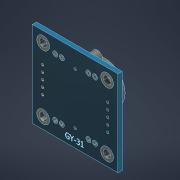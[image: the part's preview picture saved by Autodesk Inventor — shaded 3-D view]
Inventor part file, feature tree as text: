
AUTODESK INVENTOR PART (.ipt)
format: ipt  version: 2021 (Build 250183000, 183)  size: 1,518,592 bytes
history: native  units: mm
features: sketch x20, extrude x14, projected_geometry x8, hole x4, mirror x4, fillet x2, thread x1, plane x1
ambient origin geometry x8: Origin, YZ Plane, XZ Plane, XY Plane, X Axis, Y Axis, Z Axis, Center Point
bodies: Solid1 (feature_tree)
feature tree (54):
  extrude  "Extrusion1"  Depth=33.5mm
  hole  "Hole1"  [1 undecoded]
  extrude  "Extrusion2"  Depth=25.0mm
  extrude  "Extrusion3"  TaperAngle=0.0deg  [1 undecoded]
  hole  "Hole2"  [1 undecoded]
  mirror  "Mirror1"
  extrude  "Extrusion4"  Depth=5.0mm
  mirror  "Mirror2"
  extrude  "Extrusion5"  Depth=5.0mm
  mirror  "Mirror3"
  extrude  "Extrusion6"  Depth=0.01mm TaperAngle=0.0deg
  extrude  "Extrusion7"  Depth=4.0mm
  hole  "Hole3"  [1 undecoded]
  extrude  "Extrusion8"  Depth=2.0mm
  extrude  "Extrusion9"  Depth=2.0mm
  mirror  "Mirror4"
  extrude  "Extrusion10"  Depth=0.01mm TaperAngle=0.0deg
  extrude  "Extrusion11"  Depth=13.0mm
  hole  "Hole4"  [1 undecoded]
  extrude  "Extrusion12"  Depth=0.01mm TaperAngle=0.0deg
  fillet  "Fillet1"  Radius=0.01mm
  fillet  "Fillet2"  Radius=2.54mm
  extrude  "Extrusion13"  Depth=9.0mm
  extrude  "Extrusion14"  Depth=5.5mm
  sketch  "Sketch19"  dims[d62=2.54mm d63=5.5mm d64=9.0mm]
  sketch  "Sketch20"  dims[d65=1.0mm d66=6.0mm d67=4.0mm d68=2.0mm d69=90.0deg d70=8.0mm d71=20.594885mm d72=2.0mm d73=2.0mm d74=2.0mm d75=2.0mm d76=0.01mm d77=0.0mm d78=2.0mm d79=2.0mm d80=2.0mm d81=2.0mm d82=0.01mm d83=0.0mm d84=16.0mm d85=16.0mm d86=10.0mm d87=4.3mm d88=7.0mm d89=0.0mm d90=15.8mm d91=3.0mm d92=0.0mm d93=1.0mm d94=6.0mm d95=4.0mm d96=2.0mm d97=90.0deg d98=8.0mm d99=20.594885mm d100=3.5mm d101=0.9mm d102=1.5mm d103=0.0mm d104=0.0mm d105=0.02mm d106=0.02mm d107=2.14mm d108=0.9mm d109=0.0mm d111=1.0mm d112=1.0mm d113=6.4mm d114=0.0mm d115=10.0mm d116=0.0mm]
  thread  "Thread1"  [1 undecoded]
  sketch  "Sketch1"  dims[d0=33.5mm d1=33.5mm]
  sketch  "Sketch2"  dims[d2=1.65mm d3=0.0mm d4=25.0mm]
  sketch  "Sketch3"  dims[d5=25.0mm d6=25.0mm]
  projected_geometry  "Projected Loop1"
  sketch  "Sketch4"  dims[d7=25.0mm d8=0.0mm]
  projected_geometry  "Projected Loop2"
  sketch  "Sketch5"  dims[d9=4.25mm d10=4.25mm]
  plane  "Work Plane1"
  sketch  "Sketch6"  dims[d11=3.0mm d12=6.0mm d13=4.0mm d14=2.0mm d15=90.0deg d16=8.0mm d17=20.594885mm d18=5.0mm]
  projected_geometry  "Projected Loop3"
  sketch  "Sketch7"  dims[d19=5.0mm d20=5.0mm]
  sketch  "Sketch8"  dims[d21=5.0mm d22=0.01mm d23=0.0mm]
  sketch  "Sketch9"  dims[d24=0.01mm d25=0.0mm d26=4.0mm]
  sketch  "Sketch10"  dims[d27=50.0mm d29=2.54mm d30=10.0mm d32=10.0mm]
  sketch  "Sketch11"  dims[d34=1.0mm d35=6.0mm d36=4.0mm d37=2.0mm d38=90.0deg d39=8.0mm d40=20.594885mm d41=11.68mm]
  projected_geometry  "Projected Loop4"
  sketch  "Sketch12"  dims[d42=2.0mm d43=2.0mm]
  projected_geometry  "Projected Loop5"
  sketch  "Sketch13"  dims[d44=2.0mm d45=2.0mm]
  sketch  "Sketch14"  dims[d46=2.0mm d47=0.01mm d48=0.0mm]
  sketch  "Sketch15"  dims[d49=3.3mm d50=13.0mm]
  projected_geometry  "Projected Loop6"
  sketch  "Sketch16"  dims[d51=0.4mm d52=0.4mm]
  sketch  "Sketch17"  dims[d53=0.01mm d54=0.0mm d55=0.01mm d56=0.0mm d57=0.01mm d58=0.0mm d59=2.54mm]
  sketch  "Sketch18"  dims[d60=5.5mm d61=9.0mm]
  projected_geometry  "Projected Loop7"
  projected_geometry  "Projected Loop8"
note: 6 required parameter values undecoded (feature->parameter linkage not recoverable at this tier; creation-order binding heuristic only, values carry confidence <= 0.55)
